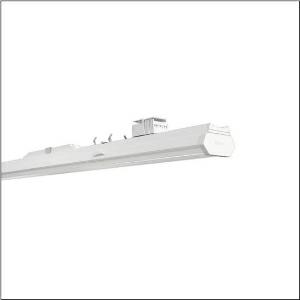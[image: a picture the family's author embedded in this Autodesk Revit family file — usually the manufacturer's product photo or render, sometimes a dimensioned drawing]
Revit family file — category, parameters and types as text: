
# Revit family: licross_r__21_protected_ho_52td13mn4fxs_5700
name_source: partatom
category: Lighting Fixtures
units: mm (PartAtom-declared; Revit-internal decimal feet)

## family parameters
Cut with Voids When Loaded = No
Host = Face
Light Source = No
Part Type = Normal
Room Calculation Point = No
Round Connector Dimension = Use Diameter
Shared = No

## types (1)
- --- (1 x LED, 15060 lm, 83.2 W, 4000K)
    Apparent Load = 83 VA
    CIE Flux Codes = 89 96 99 100 99
    Color Rendering = 80
    Color Temperature = 4000K
    Default Elevation = 1800 mm
    Description = Licross® 21 Protected HO, luminaire insert, of sheet steel, galvanised, coil coated, white, length: 1.500mm, width: 66mm, height: 67mm, LED rated luminous flux: 15.060lm, light colour: 840, control gear: ON/OFF Multilumen, with plug, 3-pole, with phase selection, mains connection: 220..240V, AC, 50/60Hz, rated input power: 83W, internal wiring halogen-free, primary light control with lens, of plastic, primary optical cover: cover, of PMMA, light emission: direct distribution, primary light characteristic: symmetric, protection rating (complete): IP54, insulation class (complete): insulation class I (protective earthing), certification: CE, ENEC, VDE, UKCA, protection symbol: D if used in an environment with non-conductive dust loads with corresponding accessories, impact resistance: IK06, permissible ambient temperature for indoor applications: -35..+35°C, corresponds to IFS (International Featured Standards) requirements for safety and quality in the food industry, reducing of maximum allowable ambient temperature of 5°C with ceiling mounting, LABS conformity tested according to VDMA 24364:2018-05, packaging unit: 1 piece
    Height = 92 mm
    Lamp = 1 x LED
    Lamp Light Flux = 15060 lm
    Lamp Power = 83.2 W
    Lamp count = 1
    Length = 1500 mm
    Luminous efficacy = 181 lm/W
    Manufacturer = Siteco
    ModVariant = No
    Model = 52TD13MN4FXS
    Mounting Place = Ceiling
    Mounting Type = Pendant
    Number of Poles = 1
    OnlyDefault = Yes
    Power Factor = 1
    Product Name = Licross® 21 Protected HO
    Product group = luminaire insert | ceiling pendant
    ProductGroupID = 902
    Protection Class = Protection class I
    Protection Degree = IP 54
    RLX_Detail_Level = 1
    RLX_Emergency_Light_Flux = 0 lm
    RLX_Emergency_Type = 0
    RLX_Emergency_Type_DB = No
    RlxData = <blob elided: 22041 chars, md5=a987a010>
    Socket = socket
    Standby Power = 0 W
    System Light Flux = 15060 lm
    System Power = 83 W
    Type Comments = factory setting: luminous flux: 100 % | (A | C | E) | 195 mA
    Type Image = l_1256148.jpg
    URL = http://relux.com
    VarID = @adj_130479
    Voltage = 0 V
    Weight = 0.00 kg
    Width = 88 mm

## geometry (parser evidence)
native form markers: Blend x4, Sweep x14
no freeform markers — native parametric forms only
